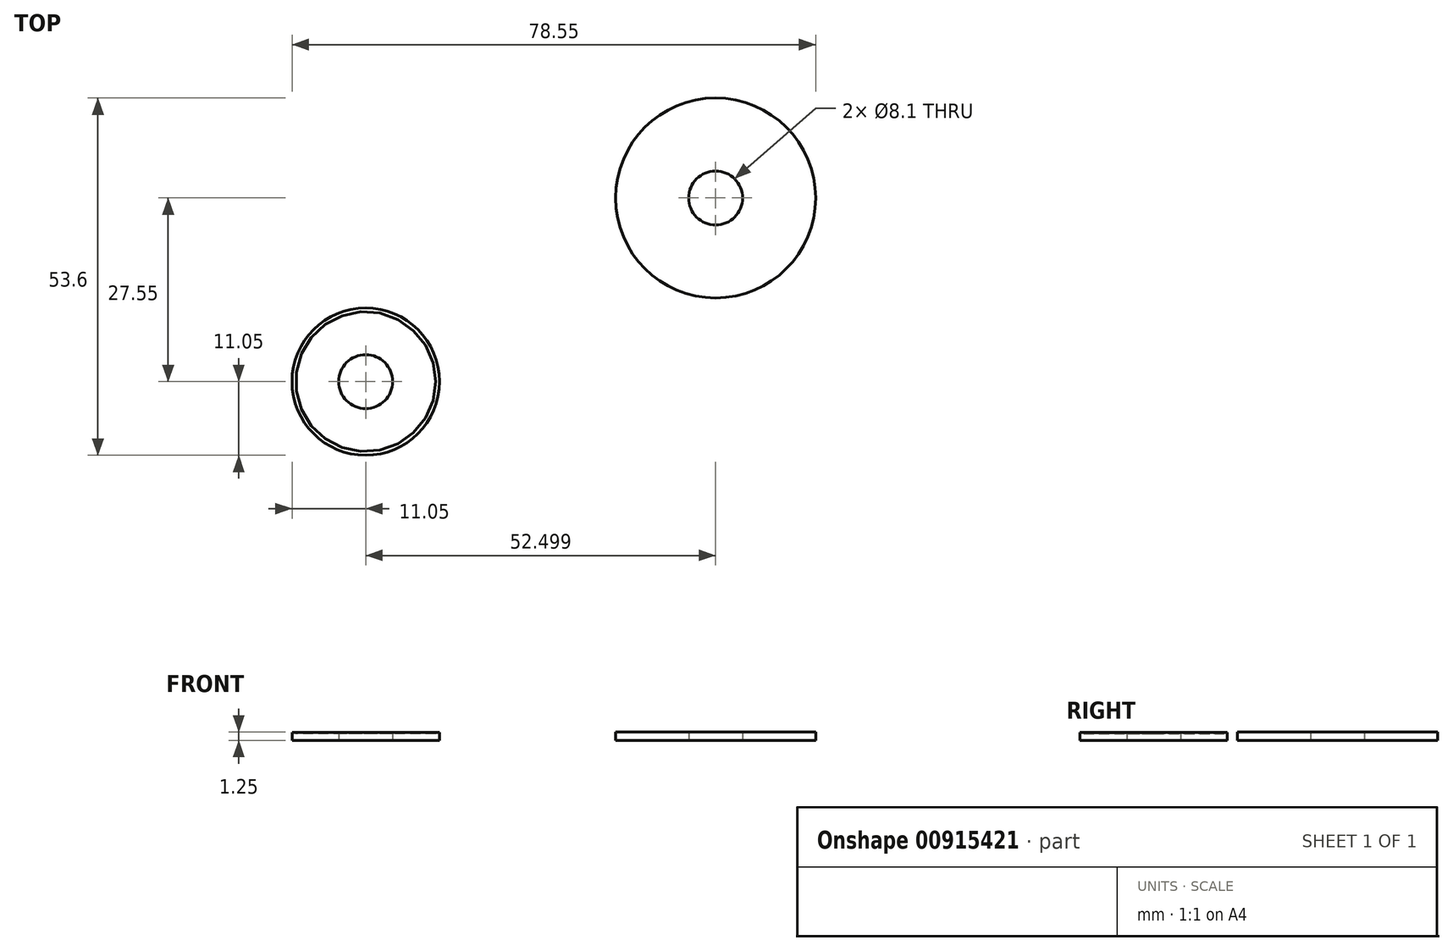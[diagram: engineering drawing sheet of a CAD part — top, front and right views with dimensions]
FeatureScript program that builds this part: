
annotation { "Feature Type Name" : "Feature", "Feature Type Description" : "" }
export const myFeature = defineFeature(function(context is Context, id is Id, definition is map)
    precondition{}
    {
        {
            var Q0;
            Q0=qCreatedBy(makeId("Top.planeOp"),FACE);
            var sketch = newSketch(context, id + "F0", { "sketchPlane" : qUnion([Q0])});
            skCircle(sketch, "E0", {"center": v(0, 0) * mm, "radius": 10.5 * mm});
            skCircle(sketch, "E1", {"center": v(0, 0) * mm, "radius": 4.05 * mm});
            skCircle(sketch, "E2", {"center": v(0, 0) * mm, "radius": 11.05 * mm});
            skCircle(sketch, "E3", {"center": v(52.5, 27.55) * mm, "radius": 15 * mm});
            skCircle(sketch, "E4", {"center": v(52.5, 27.55) * mm, "radius": 4.05 * mm});
            skSolve(sketch);
        }
        {
            var Q0;
            Q0=makeQuery(id+"F0.imprint","IMPRINT",FACE,{"disambiguationData":[TD([[makeQuery(id+"F0.imprint","IMPRINT",EDGE,{"derivedFrom":sQuery(id+"F0.wireOp",EDGE,"E0")}),1.0]])]});
            extrude(context, id + "F1", {"entities" : qUnion([Q0]), "depth" : 1 * mm, "offsetDistance" : 25 * mm});
        }
        {
            var Q0;
            Q0=makeQuery(id+"F0.imprint","IMPRINT",FACE,{"disambiguationData":[TD([[makeQuery(id+"F0.imprint","IMPRINT",EDGE,{"derivedFrom":sQuery(id+"F0.wireOp",EDGE,"E0")}),-1.0]])]});
            extrude(context, id + "F2", {"entities" : qUnion([Q0]), "operationType" : NewBodyOperationType.ADD, "depth" : 1.2 * mm, "offsetDistance" : 25 * mm});
        }
        {
            var Q0;
            Q0=makeQuery(id+"F2.opExtrude","CAP_EDGE",EDGE,{"disambiguationData":[OSD([sQuery(id+"F0.wireOp",EDGE,"E0")])],"isStart":false});
            fillet(context, id + "F3", {"entities" : qUnion([Q0]), "radius" : .5 * mm, "tangentPropagation" : true, "rho" : 0.5, "crossSection" : FilletCrossSection.CONIC, "allowEdgeOverflow" : false});
        }
        {
            var Q0;
            Q0=makeQuery(id+"F0.imprint","IMPRINT",FACE,{"disambiguationData":[TD([[makeQuery(id+"F0.imprint","IMPRINT",EDGE,{"derivedFrom":sQuery(id+"F0.wireOp",EDGE,"E3")}),1.0]])]});
            extrude(context, id + "F4", {"entities" : qUnion([Q0]), "depth" : 1.25 * mm, "offsetDistance" : 25 * mm});
        }
    });
